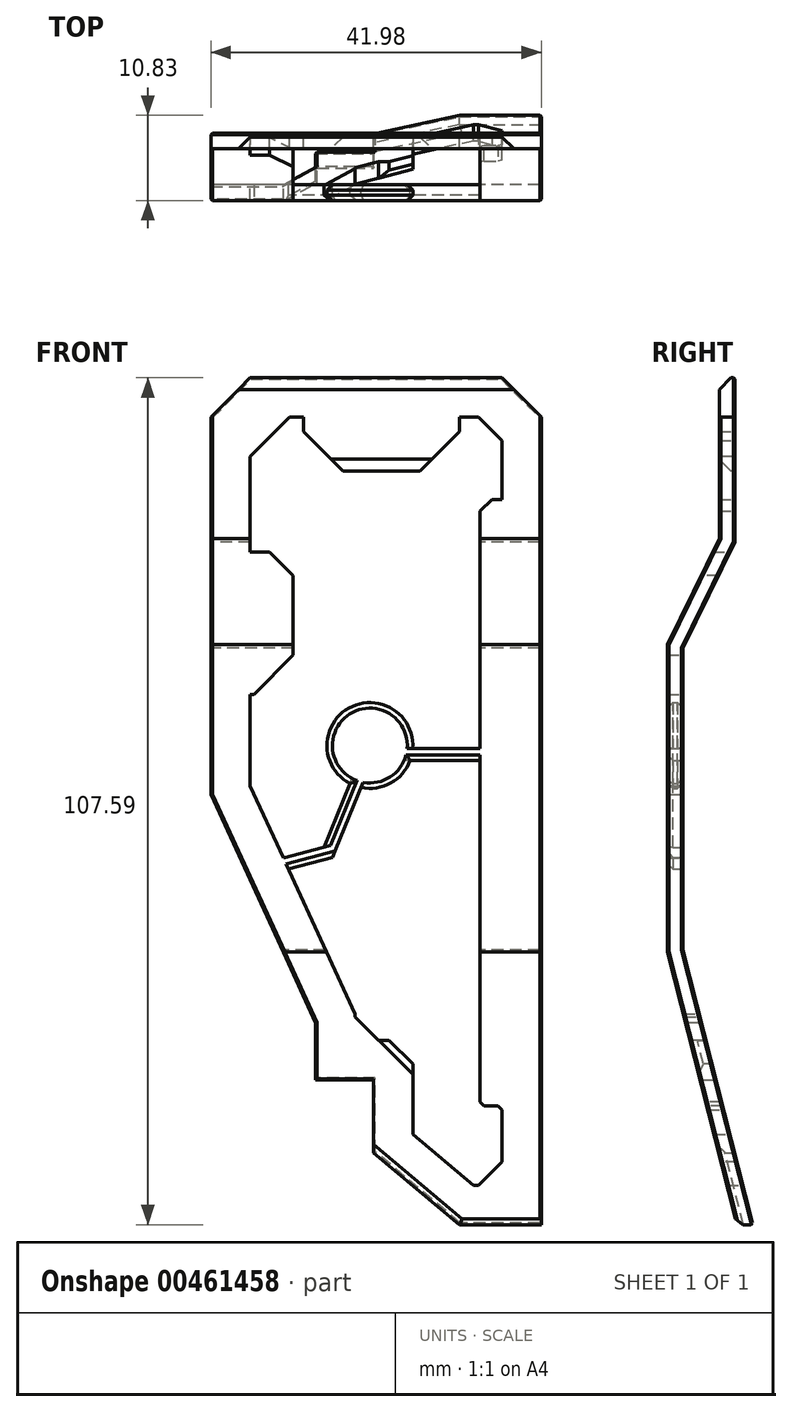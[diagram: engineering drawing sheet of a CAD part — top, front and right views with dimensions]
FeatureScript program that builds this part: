
annotation { "Feature Type Name" : "Feature", "Feature Type Description" : "" }
export const myFeature = defineFeature(function(context is Context, id is Id, definition is map)
    precondition{}
    {
        {
            var Q0;
            Q0=qCreatedBy(makeId("Front.planeOp"),FACE);
            var sketch = newSketch(context, id + "F0", { "sketchPlane" : qUnion([Q0])});
            skLineSegment(sketch, "E0", {"start": v(-31.56, 59.34) * mm, "end": v(-31.56, 0) * mm});
            skLineSegment(sketch, "E1", {"start": v(-31.56, 0) * mm, "end": v(-18.26, -28.95) * mm});
            skLineSegment(sketch, "E2", {"start": v(-18.26, -28.95) * mm, "end": v(-18.26, -36.23) * mm});
            skLineSegment(sketch, "E3", {"start": v(-18.26, -36.23) * mm, "end": v(-10.9, -36.23) * mm});
            skLineSegment(sketch, "E4", {"start": v(-10.9, -36.23) * mm, "end": v(-10.9, -45.5) * mm});
            skLineSegment(sketch, "E5", {"start": v(-10.9, -45.5) * mm, "end": v(0, -54.63) * mm});
            skLineSegment(sketch, "E6", {"start": v(0, -54.63) * mm, "end": v(10.42, -54.63) * mm});
            skLineSegment(sketch, "E7", {"start": v(10.42, -54.63) * mm, "end": v(10.42, 59.87) * mm});
            skLineSegment(sketch, "E8", {"start": v(-37.67, 52.96) * mm, "end": v(18.58, 52.96) * mm});
            skSolve(sketch);
        }
        {
            var Q0;
            Q0 = qSketchRegion(id + "F0", true);
            extrude(context, id + "F1", {"entities" : qUnion([Q0]), "depth" : 25.4 * mm});
        }
        {
            var Q0;
            Q0=qCreatedBy(makeId("Front.planeOp"),FACE);
            var sketch = newSketch(context, id + "F2", { "sketchPlane" : qUnion([Q0])});
            skLineSegment(sketch, "E9.0", {"start": v(-26.56, 47.96) * mm, "end": v(-26.56, 1.1) * mm});
            skLineSegment(sketch, "E9.1", {"start": v(-26.56, 1.1) * mm, "end": v(-13.26, -27.86) * mm});
            skLineSegment(sketch, "E9.2", {"start": v(-26.56, 47.96) * mm, "end": v(5.42, 47.96) * mm});
            skLineSegment(sketch, "E9.3", {"start": v(-13.26, -27.86) * mm, "end": v(-13.26, -31.23) * mm});
            skLineSegment(sketch, "E9.4", {"start": v(-13.26, -31.23) * mm, "end": v(-5.9, -31.23) * mm});
            skLineSegment(sketch, "E9.5", {"start": v(5.42, -49.63) * mm, "end": v(5.42, 47.96) * mm});
            skLineSegment(sketch, "E9.6", {"start": v(1.82, -49.63) * mm, "end": v(5.42, -49.63) * mm});
            skLineSegment(sketch, "E9.7", {"start": v(-5.9, -43.16) * mm, "end": v(1.82, -49.63) * mm});
            skLineSegment(sketch, "E9.8", {"start": v(-5.9, -31.23) * mm, "end": v(-5.9, -43.16) * mm});
            skLineSegment(sketch, "E10.bottom", {"start": v(-19.8, 63.96) * mm, "end": v(0, 63.96) * mm});
            skLineSegment(sketch, "E10.top", {"start": v(-19.8, 41.13) * mm, "end": v(0, 41.13) * mm});
            skLineSegment(sketch, "E10.left", {"start": v(-19.8, 63.96) * mm, "end": v(-19.8, 41.13) * mm});
            skLineSegment(sketch, "E10.right", {"start": v(0, 63.96) * mm, "end": v(0, 41.13) * mm});
            skLineSegment(sketch, "E11.bottom", {"start": v(-36.17, 30.84) * mm, "end": v(-21.1, 30.84) * mm});
            skLineSegment(sketch, "E11.top", {"start": v(-36.17, 12.73) * mm, "end": v(-21.1, 12.73) * mm});
            skLineSegment(sketch, "E11.left", {"start": v(-36.17, 30.84) * mm, "end": v(-36.17, 12.73) * mm});
            skLineSegment(sketch, "E11.right", {"start": v(-21.1, 30.84) * mm, "end": v(-21.1, 12.73) * mm});
            skLineSegment(sketch, "E12.bottom", {"start": v(15.3, -39.52) * mm, "end": v(2.65, -39.52) * mm});
            skLineSegment(sketch, "E12.top", {"start": v(15.3, 37.5) * mm, "end": v(2.65, 37.5) * mm});
            skLineSegment(sketch, "E12.left", {"start": v(15.3, -39.52) * mm, "end": v(15.3, 37.5) * mm});
            skLineSegment(sketch, "E12.right", {"start": v(2.65, -39.52) * mm, "end": v(2.65, 37.5) * mm});
            skCircle(sketch, "E13", {"center": v(-11.36, 6.24) * mm, "radius": 5.46 * mm});
            skLineSegment(sketch, "E14", {"start": v(-29.17, -9.83) * mm, "end": v(-17.21, -6.7) * mm});
            skLineSegment(sketch, "E15", {"start": v(-17.21, -6.7) * mm, "end": v(-12.54, 4.7) * mm});
            skLineSegment(sketch, "E16", {"start": v(-9.3, 5.86) * mm, "end": v(5.42, 5.86) * mm});
            skLineSegment(sketch, "E17.0", {"start": v(-16.11, -7.97) * mm, "end": v(-11.15, 4.13) * mm});
            skLineSegment(sketch, "E17.1", {"start": v(-28.8, -11.29) * mm, "end": v(-16.11, -7.97) * mm});
            skLineSegment(sketch, "E18.0", {"start": v(-9.3, 4.36) * mm, "end": v(5.42, 4.36) * mm});
            skLineSegment(sketch, "E19", {"start": v(-12.54, 4.7) * mm, "end": v(-11.15, 4.13) * mm});
            skLineSegment(sketch, "E20", {"start": v(-9.3, 5.86) * mm, "end": v(-9.3, 4.36) * mm});
            skLineSegment(sketch, "E21", {"start": v(-29.17, -9.83) * mm, "end": v(-29.17, -9.83) * mm});
            skLineSegment(sketch, "E22", {"start": v(-29.17, -9.83) * mm, "end": v(-28.8, -11.29) * mm});
            skLineSegment(sketch, "E23", {"start": v(5.42, 5.86) * mm, "end": v(5.42, 4.36) * mm});
            skSolve(sketch);
        }
        {
            var Q0;
            {var subQ1=sQuery(id+"F2.wireOp",EDGE,"E10.top");Q0=makeQuery(id+"F2.imprint","IMPRINT",FACE,{"disambiguationData":[TD([[makeQuery(id+"F2.imprint","IMPRINT",EDGE,{"derivedFrom":subQ1}),-1.0]])]});}
            extrude(context, id + "F3", {"entities" : qUnion([Q0]), "endBound" : BoundingType.SYMMETRIC, "depth" : 60 * mm});
        }
        {
            var Q0;
            {var subQ10=sQuery(id+"F2.wireOp",EDGE,"E9.3");Q0=makeQuery(id+"F2.imprint","IMPRINT",FACE,{"disambiguationData":[TD([[makeQuery(id+"F2.imprint","IMPRINT",EDGE,{"derivedFrom":subQ10}),1.0]])]});}
            extrude(context, id + "F4", {"entities" : qUnion([Q0]), "endBound" : BoundingType.SYMMETRIC, "depth" : 60 * mm});
        }
        {
            var Q0;
            Q0=makeQuery(id+"F3.opExtrude","SWEPT_BODY",BODY,{"disambiguationData":[OSD([sQuery(id+"F2.wireOp",EDGE,"E9.0"),sQuery(id+"F2.wireOp",EDGE,"E9.1"),sQuery(id+"F2.wireOp",EDGE,"E9.2"),sQuery(id+"F2.wireOp",EDGE,"E9.5"),sQuery(id+"F2.wireOp",EDGE,"E10.top"),sQuery(id+"F2.wireOp",EDGE,"E10.left"),sQuery(id+"F2.wireOp",EDGE,"E10.right"),sQuery(id+"F2.wireOp",EDGE,"E11.bottom"),sQuery(id+"F2.wireOp",EDGE,"E11.top"),sQuery(id+"F2.wireOp",EDGE,"E11.right"),sQuery(id+"F2.wireOp",EDGE,"E12.top"),sQuery(id+"F2.wireOp",EDGE,"E12.right"),sQuery(id+"F2.wireOp",EDGE,"E13"),sQuery(id+"F2.wireOp",EDGE,"E14"),sQuery(id+"F2.wireOp",EDGE,"E15"),sQuery(id+"F2.wireOp",EDGE,"E16")])]});
            var Q1;
            Q1=makeQuery(id+"F1.opExtrude","SWEPT_BODY",BODY,{"disambiguationData":[OSD([sQuery(id+"F0.wireOp",EDGE,"E0"),sQuery(id+"F0.wireOp",EDGE,"E1"),sQuery(id+"F0.wireOp",EDGE,"E2"),sQuery(id+"F0.wireOp",EDGE,"E3"),sQuery(id+"F0.wireOp",EDGE,"E4"),sQuery(id+"F0.wireOp",EDGE,"E5"),sQuery(id+"F0.wireOp",EDGE,"E6"),sQuery(id+"F0.wireOp",EDGE,"E7"),sQuery(id+"F0.wireOp",EDGE,"E8")])]});
            booleanBodies(context, id + "F5", {"operationType" : BooleanOperationType.SUBTRACTION, "tools" : qUnion([Q0]), "targets" : qUnion([Q1])});
        }
        {
            var Q0;
            Q0=makeQuery(id+"F4.opExtrude","SWEPT_BODY",BODY,{"disambiguationData":[OSD([sQuery(id+"F2.wireOp",EDGE,"E9.1"),sQuery(id+"F2.wireOp",EDGE,"E9.3"),sQuery(id+"F2.wireOp",EDGE,"E9.4"),sQuery(id+"F2.wireOp",EDGE,"E9.5"),sQuery(id+"F2.wireOp",EDGE,"E9.6"),sQuery(id+"F2.wireOp",EDGE,"E9.7"),sQuery(id+"F2.wireOp",EDGE,"E9.8"),sQuery(id+"F2.wireOp",EDGE,"E12.bottom"),sQuery(id+"F2.wireOp",EDGE,"E12.right"),sQuery(id+"F2.wireOp",EDGE,"E13"),sQuery(id+"F2.wireOp",EDGE,"E17.0"),sQuery(id+"F2.wireOp",EDGE,"E17.1"),sQuery(id+"F2.wireOp",EDGE,"E18.0")])]});
            var Q1;
            Q1=makeQuery(id+"F1.opExtrude","SWEPT_BODY",BODY,{"disambiguationData":[OSD([sQuery(id+"F0.wireOp",EDGE,"E0"),sQuery(id+"F0.wireOp",EDGE,"E1"),sQuery(id+"F0.wireOp",EDGE,"E2"),sQuery(id+"F0.wireOp",EDGE,"E3"),sQuery(id+"F0.wireOp",EDGE,"E4"),sQuery(id+"F0.wireOp",EDGE,"E5"),sQuery(id+"F0.wireOp",EDGE,"E6"),sQuery(id+"F0.wireOp",EDGE,"E7"),sQuery(id+"F0.wireOp",EDGE,"E8")])]});
            booleanBodies(context, id + "F6", {"operationType" : BooleanOperationType.SUBTRACTION, "tools" : qUnion([Q0]), "targets" : qUnion([Q1])});
        }
        {
            var Q0;
            Q0=makeQuery(id+"F1.opExtrude","CAP_FACE",FACE,{"disambiguationData":[OSD([sQuery(id+"F0.wireOp",EDGE,"E0"),sQuery(id+"F0.wireOp",EDGE,"E1"),sQuery(id+"F0.wireOp",EDGE,"E2"),sQuery(id+"F0.wireOp",EDGE,"E3"),sQuery(id+"F0.wireOp",EDGE,"E4"),sQuery(id+"F0.wireOp",EDGE,"E5"),sQuery(id+"F0.wireOp",EDGE,"E6"),sQuery(id+"F0.wireOp",EDGE,"E7"),sQuery(id+"F0.wireOp",EDGE,"E8")])],"isStart":true});
            extrude(context, id + "F7", {"entities" : qUnion([Q0]), "operationType" : NewBodyOperationType.ADD, "depth" : 25 * mm});
        }
        {
            var Q0;
            Q0=qCreatedBy(makeId("Right.planeOp"),FACE);
            var sketch = newSketch(context, id + "F8", { "sketchPlane" : qUnion([Q0])});
            skLineSegment(sketch, "E24", {"start": v(-5.44, 63.21) * mm, "end": v(-5.44, 32.1) * mm});
            skLineSegment(sketch, "E25", {"start": v(-5.44, 32.1) * mm, "end": v(-12.03, 18.6) * mm});
            skLineSegment(sketch, "E26", {"start": v(-12.03, 18.6) * mm, "end": v(-12.03, -19.71) * mm});
            skLineSegment(sketch, "E27", {"start": v(-12.03, -19.71) * mm, "end": v(-1.98, -59.15) * mm});
            skLineSegment(sketch, "E28.0", {"start": v(-14.03, -19.96) * mm, "end": v(-3.92, -59.64) * mm});
            skLineSegment(sketch, "E28.1", {"start": v(-14.03, 19.06) * mm, "end": v(-14.03, -19.96) * mm});
            skLineSegment(sketch, "E28.2", {"start": v(-7.44, 32.55) * mm, "end": v(-14.03, 19.06) * mm});
            skLineSegment(sketch, "E28.3", {"start": v(-7.44, 63.21) * mm, "end": v(-7.44, 32.55) * mm});
            skLineSegment(sketch, "E29", {"start": v(-5.44, 63.21) * mm, "end": v(-7.44, 63.21) * mm});
            skLineSegment(sketch, "E30", {"start": v(-1.98, -59.15) * mm, "end": v(-3.92, -59.64) * mm});
            skSolve(sketch);
        }
        {
            var Q0;
            Q0=makeQuery(id+"F8.imprint","IMPRINT",FACE,{"disambiguationData":[TD([[makeQuery(id+"F8.imprint","IMPRINT",EDGE,{"derivedFrom":sQuery(id+"F8.wireOp",EDGE,"E24")}),-1.0]])]});
            extrude(context, id + "F9", {"entities" : qUnion([Q0]), "endBound" : BoundingType.SYMMETRIC, "depth" : 80 * mm});
        }
        {
            var Q0;
            Q0=makeQuery(id+"F1.opExtrude","SWEPT_BODY",BODY,{"disambiguationData":[OSD([sQuery(id+"F0.wireOp",EDGE,"E0"),sQuery(id+"F0.wireOp",EDGE,"E1"),sQuery(id+"F0.wireOp",EDGE,"E2"),sQuery(id+"F0.wireOp",EDGE,"E3"),sQuery(id+"F0.wireOp",EDGE,"E4"),sQuery(id+"F0.wireOp",EDGE,"E5"),sQuery(id+"F0.wireOp",EDGE,"E6"),sQuery(id+"F0.wireOp",EDGE,"E7"),sQuery(id+"F0.wireOp",EDGE,"E8")])]});
            var Q1;
            Q1=makeQuery(id+"F9.opExtrude","SWEPT_BODY",BODY,{"disambiguationData":[OSD([sQuery(id+"F8.wireOp",EDGE,"E24"),sQuery(id+"F8.wireOp",EDGE,"E25"),sQuery(id+"F8.wireOp",EDGE,"E26"),sQuery(id+"F8.wireOp",EDGE,"E27"),sQuery(id+"F8.wireOp",EDGE,"E28.0"),sQuery(id+"F8.wireOp",EDGE,"E28.1"),sQuery(id+"F8.wireOp",EDGE,"E28.2"),sQuery(id+"F8.wireOp",EDGE,"E28.3"),sQuery(id+"F8.wireOp",EDGE,"E29"),sQuery(id+"F8.wireOp",EDGE,"E30")])]});
            booleanBodies(context, id + "F10", {"operationType" : BooleanOperationType.INTERSECTION, "tools" : qUnion([Q0, Q1])});
        }
        {
            var Q0;
            {var subQ0=sQuery(id+"F2.wireOp",EDGE,"E9.2");var subQ1=sQuery(id+"F2.wireOp",EDGE,"E9.0");Q0=makeQuery(id+"F7.boolean.opBoolean","MERGE",EDGE,{"derivedFrom":[makeQuery(id+"F5.opBoolean","COPY",EDGE,{"derivedFrom":makeQuery(id+"F3.opExtrude","SWEPT_EDGE",EDGE,{"disambiguationData":[OSD([subQ1,subQ0])]})}),makeQuery(id+"F7.opExtrude","SWEPT_EDGE",EDGE,{"disambiguationData":[OSD([sQuery(id+"F0.wireOp",EDGE,"E0"),sQuery(id+"F0.wireOp",EDGE,"E1"),sQuery(id+"F0.wireOp",EDGE,"E2"),sQuery(id+"F0.wireOp",EDGE,"E3"),sQuery(id+"F0.wireOp",EDGE,"E4"),sQuery(id+"F0.wireOp",EDGE,"E5"),sQuery(id+"F0.wireOp",EDGE,"E6"),sQuery(id+"F0.wireOp",EDGE,"E7"),sQuery(id+"F0.wireOp",EDGE,"E8"),subQ1,subQ0])]})]});}
            var Q1;
            {var subQ0=sQuery(id+"F2.wireOp",EDGE,"E10.right");var subQ1=sQuery(id+"F2.wireOp",EDGE,"E10.top");Q1=makeQuery(id+"F7.boolean.opBoolean","MERGE",EDGE,{"derivedFrom":[makeQuery(id+"F5.opBoolean","COPY",EDGE,{"derivedFrom":makeQuery(id+"F3.opExtrude","SWEPT_EDGE",EDGE,{"disambiguationData":[OSD([subQ1,subQ0])]})}),makeQuery(id+"F7.opExtrude","SWEPT_EDGE",EDGE,{"disambiguationData":[OSD([sQuery(id+"F0.wireOp",EDGE,"E0"),sQuery(id+"F0.wireOp",EDGE,"E1"),sQuery(id+"F0.wireOp",EDGE,"E2"),sQuery(id+"F0.wireOp",EDGE,"E3"),sQuery(id+"F0.wireOp",EDGE,"E4"),sQuery(id+"F0.wireOp",EDGE,"E5"),sQuery(id+"F0.wireOp",EDGE,"E6"),sQuery(id+"F0.wireOp",EDGE,"E7"),sQuery(id+"F0.wireOp",EDGE,"E8"),subQ1,subQ0])]})]});}
            var Q2;
            {var subQ0=sQuery(id+"F2.wireOp",EDGE,"E10.left");var subQ1=sQuery(id+"F2.wireOp",EDGE,"E10.top");Q2=makeQuery(id+"F7.boolean.opBoolean","MERGE",EDGE,{"derivedFrom":[makeQuery(id+"F5.opBoolean","COPY",EDGE,{"derivedFrom":makeQuery(id+"F3.opExtrude","SWEPT_EDGE",EDGE,{"disambiguationData":[OSD([subQ1,subQ0])]})}),makeQuery(id+"F7.opExtrude","SWEPT_EDGE",EDGE,{"disambiguationData":[OSD([sQuery(id+"F0.wireOp",EDGE,"E0"),sQuery(id+"F0.wireOp",EDGE,"E1"),sQuery(id+"F0.wireOp",EDGE,"E2"),sQuery(id+"F0.wireOp",EDGE,"E3"),sQuery(id+"F0.wireOp",EDGE,"E4"),sQuery(id+"F0.wireOp",EDGE,"E5"),sQuery(id+"F0.wireOp",EDGE,"E6"),sQuery(id+"F0.wireOp",EDGE,"E7"),sQuery(id+"F0.wireOp",EDGE,"E8"),subQ1,subQ0])]})]});}
            var Q3;
            {var subQ0=sQuery(id+"F2.wireOp",EDGE,"E11.right");var subQ1=sQuery(id+"F2.wireOp",EDGE,"E11.top");Q3=makeQuery(id+"F7.boolean.opBoolean","MERGE",EDGE,{"derivedFrom":[makeQuery(id+"F5.opBoolean","COPY",EDGE,{"derivedFrom":makeQuery(id+"F3.opExtrude","SWEPT_EDGE",EDGE,{"disambiguationData":[OSD([subQ1,subQ0])]})}),makeQuery(id+"F7.opExtrude","SWEPT_EDGE",EDGE,{"disambiguationData":[OSD([sQuery(id+"F0.wireOp",EDGE,"E0"),sQuery(id+"F0.wireOp",EDGE,"E1"),sQuery(id+"F0.wireOp",EDGE,"E2"),sQuery(id+"F0.wireOp",EDGE,"E3"),sQuery(id+"F0.wireOp",EDGE,"E4"),sQuery(id+"F0.wireOp",EDGE,"E5"),sQuery(id+"F0.wireOp",EDGE,"E6"),sQuery(id+"F0.wireOp",EDGE,"E7"),sQuery(id+"F0.wireOp",EDGE,"E8"),subQ1,subQ0])]})]});}
            chamfer(context, id + "F11", {"entities" : qUnion([Q0, Q1, Q2, Q3]), "width" : 5 * mm, "tangentPropagation" : true});
        }
        {
            var Q0;
            {var subQ0=sQuery(id+"F2.wireOp",EDGE,"E9.5");var subQ1=sQuery(id+"F2.wireOp",EDGE,"E9.2");Q0=makeQuery(id+"F7.boolean.opBoolean","MERGE",EDGE,{"derivedFrom":[makeQuery(id+"F5.opBoolean","COPY",EDGE,{"derivedFrom":makeQuery(id+"F3.opExtrude","SWEPT_EDGE",EDGE,{"disambiguationData":[OSD([subQ1,subQ0])]})}),makeQuery(id+"F7.opExtrude","SWEPT_EDGE",EDGE,{"disambiguationData":[OSD([sQuery(id+"F0.wireOp",EDGE,"E0"),sQuery(id+"F0.wireOp",EDGE,"E1"),sQuery(id+"F0.wireOp",EDGE,"E2"),sQuery(id+"F0.wireOp",EDGE,"E3"),sQuery(id+"F0.wireOp",EDGE,"E4"),sQuery(id+"F0.wireOp",EDGE,"E5"),sQuery(id+"F0.wireOp",EDGE,"E6"),sQuery(id+"F0.wireOp",EDGE,"E7"),sQuery(id+"F0.wireOp",EDGE,"E8"),subQ1,subQ0])]})]});}
            var Q1;
            {var subQ0=sQuery(id+"F2.wireOp",EDGE,"E11.right");var subQ1=sQuery(id+"F2.wireOp",EDGE,"E11.bottom");Q1=makeQuery(id+"F7.boolean.opBoolean","MERGE",EDGE,{"derivedFrom":[makeQuery(id+"F5.opBoolean","COPY",EDGE,{"derivedFrom":makeQuery(id+"F3.opExtrude","SWEPT_EDGE",EDGE,{"disambiguationData":[OSD([subQ1,subQ0])]})}),makeQuery(id+"F7.opExtrude","SWEPT_EDGE",EDGE,{"disambiguationData":[OSD([sQuery(id+"F0.wireOp",EDGE,"E0"),sQuery(id+"F0.wireOp",EDGE,"E1"),sQuery(id+"F0.wireOp",EDGE,"E2"),sQuery(id+"F0.wireOp",EDGE,"E3"),sQuery(id+"F0.wireOp",EDGE,"E4"),sQuery(id+"F0.wireOp",EDGE,"E5"),sQuery(id+"F0.wireOp",EDGE,"E6"),sQuery(id+"F0.wireOp",EDGE,"E7"),sQuery(id+"F0.wireOp",EDGE,"E8"),subQ1,subQ0])]})]});}
            var Q2;
            {var subQ0=sQuery(id+"F2.wireOp",EDGE,"E9.6");var subQ1=sQuery(id+"F2.wireOp",EDGE,"E9.5");Q2=makeQuery(id+"F7.boolean.opBoolean","MERGE",EDGE,{"derivedFrom":[makeQuery(id+"F6.opBoolean","COPY",EDGE,{"derivedFrom":makeQuery(id+"F4.opExtrude","SWEPT_EDGE",EDGE,{"disambiguationData":[OSD([subQ1,subQ0])]})}),makeQuery(id+"F7.opExtrude","SWEPT_EDGE",EDGE,{"disambiguationData":[OSD([sQuery(id+"F0.wireOp",EDGE,"E0"),sQuery(id+"F0.wireOp",EDGE,"E1"),sQuery(id+"F0.wireOp",EDGE,"E2"),sQuery(id+"F0.wireOp",EDGE,"E3"),sQuery(id+"F0.wireOp",EDGE,"E4"),sQuery(id+"F0.wireOp",EDGE,"E5"),sQuery(id+"F0.wireOp",EDGE,"E6"),sQuery(id+"F0.wireOp",EDGE,"E7"),sQuery(id+"F0.wireOp",EDGE,"E8"),subQ1,subQ0])]})]});}
            var Q3;
            {var subQ0=sQuery(id+"F2.wireOp",EDGE,"E9.8");var subQ1=sQuery(id+"F2.wireOp",EDGE,"E9.4");Q3=makeQuery(id+"F7.boolean.opBoolean","MERGE",EDGE,{"derivedFrom":[makeQuery(id+"F6.opBoolean","COPY",EDGE,{"derivedFrom":makeQuery(id+"F4.opExtrude","SWEPT_EDGE",EDGE,{"disambiguationData":[OSD([subQ1,subQ0])]})}),makeQuery(id+"F7.opExtrude","SWEPT_EDGE",EDGE,{"disambiguationData":[OSD([sQuery(id+"F0.wireOp",EDGE,"E0"),sQuery(id+"F0.wireOp",EDGE,"E1"),sQuery(id+"F0.wireOp",EDGE,"E2"),sQuery(id+"F0.wireOp",EDGE,"E3"),sQuery(id+"F0.wireOp",EDGE,"E4"),sQuery(id+"F0.wireOp",EDGE,"E5"),sQuery(id+"F0.wireOp",EDGE,"E6"),sQuery(id+"F0.wireOp",EDGE,"E7"),sQuery(id+"F0.wireOp",EDGE,"E8"),subQ1,subQ0])]})]});}
            var Q4;
            {var subQ0=sQuery(id+"F2.wireOp",EDGE,"E9.4");var subQ1=sQuery(id+"F2.wireOp",EDGE,"E9.3");Q4=makeQuery(id+"F7.boolean.opBoolean","MERGE",EDGE,{"derivedFrom":[makeQuery(id+"F6.opBoolean","COPY",EDGE,{"derivedFrom":makeQuery(id+"F4.opExtrude","SWEPT_EDGE",EDGE,{"disambiguationData":[OSD([subQ1,subQ0])]})}),makeQuery(id+"F7.opExtrude","SWEPT_EDGE",EDGE,{"disambiguationData":[OSD([sQuery(id+"F0.wireOp",EDGE,"E0"),sQuery(id+"F0.wireOp",EDGE,"E1"),sQuery(id+"F0.wireOp",EDGE,"E2"),sQuery(id+"F0.wireOp",EDGE,"E3"),sQuery(id+"F0.wireOp",EDGE,"E4"),sQuery(id+"F0.wireOp",EDGE,"E5"),sQuery(id+"F0.wireOp",EDGE,"E6"),sQuery(id+"F0.wireOp",EDGE,"E7"),sQuery(id+"F0.wireOp",EDGE,"E8"),subQ1,subQ0])]})]});}
            chamfer(context, id + "F12", {"entities" : qUnion([Q0, Q1, Q2, Q3, Q4]), "width" : 3 * mm, "tangentPropagation" : true});
        }
        {
            var Q0;
            {var subQ0=sQuery(id+"F2.wireOp",EDGE,"E12.right");var subQ1=sQuery(id+"F2.wireOp",EDGE,"E12.top");Q0=makeQuery(id+"F7.boolean.opBoolean","MERGE",EDGE,{"derivedFrom":[makeQuery(id+"F5.opBoolean","COPY",EDGE,{"derivedFrom":makeQuery(id+"F3.opExtrude","SWEPT_EDGE",EDGE,{"disambiguationData":[OSD([subQ1,subQ0])]})}),makeQuery(id+"F7.opExtrude","SWEPT_EDGE",EDGE,{"disambiguationData":[OSD([sQuery(id+"F0.wireOp",EDGE,"E0"),sQuery(id+"F0.wireOp",EDGE,"E1"),sQuery(id+"F0.wireOp",EDGE,"E2"),sQuery(id+"F0.wireOp",EDGE,"E3"),sQuery(id+"F0.wireOp",EDGE,"E4"),sQuery(id+"F0.wireOp",EDGE,"E5"),sQuery(id+"F0.wireOp",EDGE,"E6"),sQuery(id+"F0.wireOp",EDGE,"E7"),sQuery(id+"F0.wireOp",EDGE,"E8"),subQ1,subQ0])]})]});}
            chamfer(context, id + "F13", {"entities" : qUnion([Q0]), "width" : 1.5 * mm, "tangentPropagation" : true});
        }
        {
            var Q0;
            {var subQ0=sQuery(id+"F0.wireOp",EDGE,"E8");var subQ1=sQuery(id+"F0.wireOp",EDGE,"E7");Q0=makeQuery(id+"F7.boolean.opBoolean","MERGE",EDGE,{"derivedFrom":[makeQuery(id+"F1.opExtrude","SWEPT_EDGE",EDGE,{"disambiguationData":[OSD([subQ1,subQ0])]}),makeQuery(id+"F7.opExtrude","SWEPT_EDGE",EDGE,{"disambiguationData":[OSD([subQ1,subQ0])]})]});}
            var Q1;
            {var subQ0=sQuery(id+"F0.wireOp",EDGE,"E8");var subQ1=sQuery(id+"F0.wireOp",EDGE,"E0");Q1=makeQuery(id+"F7.boolean.opBoolean","MERGE",EDGE,{"derivedFrom":[makeQuery(id+"F1.opExtrude","SWEPT_EDGE",EDGE,{"disambiguationData":[OSD([subQ1,subQ0])]}),makeQuery(id+"F7.opExtrude","SWEPT_EDGE",EDGE,{"disambiguationData":[OSD([subQ1,subQ0])]})]});}
            chamfer(context, id + "F14", {"entities" : qUnion([Q0, Q1]), "width" : 5 * mm, "tangentPropagation" : true});
        }
        {
            var Q0;
            {var subQ0=sQuery(id+"F2.wireOp",EDGE,"E13");var subQ1=makeQuery(id+"F3.opExtrude","SWEPT_FACE",FACE,{"disambiguationData":[OSD([subQ0])]});var subQ2=sQuery(id+"F0.wireOp",EDGE,"E8");var subQ3=sQuery(id+"F0.wireOp",EDGE,"E7");var subQ4=sQuery(id+"F0.wireOp",EDGE,"E6");var subQ5=sQuery(id+"F0.wireOp",EDGE,"E5");var subQ6=sQuery(id+"F0.wireOp",EDGE,"E4");var subQ7=sQuery(id+"F0.wireOp",EDGE,"E3");var subQ8=sQuery(id+"F0.wireOp",EDGE,"E2");var subQ9=sQuery(id+"F0.wireOp",EDGE,"E1");var subQ10=sQuery(id+"F0.wireOp",EDGE,"E0");Q0=makeQuery(id+"F10.opBoolean","INTERSECT",EDGE,{"derivedFrom":[makeQuery(id+"F7.boolean.opBoolean","MERGE",FACE,{"derivedFrom":[makeQuery(id+"F5.opBoolean","COPY",FACE,{"derivedFrom":subQ1}),makeQuery(id+"F7.opExtrude","SWEPT_FACE",FACE,{"disambiguationData":[OSD([subQ10,subQ9,subQ8,subQ7,subQ6,subQ5,subQ4,subQ3,subQ2,subQ0]),TDD([makeQuery(id+"F5.opBoolean","INTERSECT",EDGE,{"derivedFrom":[makeQuery(id+"F1.opExtrude","CAP_FACE",FACE,{"disambiguationData":[OSD([subQ10,subQ9,subQ8,subQ7,subQ6,subQ5,subQ4,subQ3,subQ2])],"isStart":true}),subQ1]})])]})]}),makeQuery(id+"F9.opExtrude","SWEPT_FACE",FACE,{"disambiguationData":[OSD([sQuery(id+"F8.wireOp",EDGE,"E26")])]})]});}
            var Q1;
            {var subQ0=sQuery(id+"F0.wireOp",EDGE,"E8");var subQ1=sQuery(id+"F0.wireOp",EDGE,"E7");var subQ2=sQuery(id+"F0.wireOp",EDGE,"E6");var subQ3=sQuery(id+"F0.wireOp",EDGE,"E5");var subQ4=sQuery(id+"F0.wireOp",EDGE,"E4");var subQ5=sQuery(id+"F0.wireOp",EDGE,"E3");var subQ6=sQuery(id+"F0.wireOp",EDGE,"E2");var subQ7=sQuery(id+"F0.wireOp",EDGE,"E1");var subQ8=sQuery(id+"F0.wireOp",EDGE,"E0");var subQ9=sQuery(id+"F2.wireOp",EDGE,"E13");var subQ10=makeQuery(id+"F4.opExtrude","SWEPT_FACE",FACE,{"disambiguationData":[OSD([subQ9])]});Q1=makeQuery(id+"F10.opBoolean","INTERSECT",EDGE,{"derivedFrom":[makeQuery(id+"F7.boolean.opBoolean","MERGE",FACE,{"derivedFrom":[makeQuery(id+"F6.opBoolean","COPY",FACE,{"derivedFrom":subQ10}),makeQuery(id+"F7.opExtrude","SWEPT_FACE",FACE,{"disambiguationData":[OSD([subQ8,subQ7,subQ6,subQ5,subQ4,subQ3,subQ2,subQ1,subQ0,subQ9]),TDD([makeQuery(id+"F6.opBoolean","INTERSECT",EDGE,{"derivedFrom":[subQ10,makeQuery(id+"F1.opExtrude","CAP_FACE",FACE,{"disambiguationData":[OSD([subQ8,subQ7,subQ6,subQ5,subQ4,subQ3,subQ2,subQ1,subQ0])],"isStart":true})]})])]})]}),makeQuery(id+"F9.opExtrude","SWEPT_FACE",FACE,{"disambiguationData":[OSD([sQuery(id+"F8.wireOp",EDGE,"E26")])]})]});}
            var Q2;
            {var subQ0=sQuery(id+"F2.wireOp",EDGE,"E13");var subQ1=makeQuery(id+"F3.opExtrude","SWEPT_FACE",FACE,{"disambiguationData":[OSD([subQ0])]});var subQ2=sQuery(id+"F0.wireOp",EDGE,"E8");var subQ3=sQuery(id+"F0.wireOp",EDGE,"E7");var subQ4=sQuery(id+"F0.wireOp",EDGE,"E6");var subQ5=sQuery(id+"F0.wireOp",EDGE,"E5");var subQ6=sQuery(id+"F0.wireOp",EDGE,"E4");var subQ7=sQuery(id+"F0.wireOp",EDGE,"E3");var subQ8=sQuery(id+"F0.wireOp",EDGE,"E2");var subQ9=sQuery(id+"F0.wireOp",EDGE,"E1");var subQ10=sQuery(id+"F0.wireOp",EDGE,"E0");Q2=makeQuery(id+"F10.opBoolean","INTERSECT",EDGE,{"derivedFrom":[makeQuery(id+"F7.boolean.opBoolean","MERGE",FACE,{"derivedFrom":[makeQuery(id+"F5.opBoolean","COPY",FACE,{"derivedFrom":subQ1}),makeQuery(id+"F7.opExtrude","SWEPT_FACE",FACE,{"disambiguationData":[OSD([subQ10,subQ9,subQ8,subQ7,subQ6,subQ5,subQ4,subQ3,subQ2,subQ0]),TDD([makeQuery(id+"F5.opBoolean","INTERSECT",EDGE,{"derivedFrom":[makeQuery(id+"F1.opExtrude","CAP_FACE",FACE,{"disambiguationData":[OSD([subQ10,subQ9,subQ8,subQ7,subQ6,subQ5,subQ4,subQ3,subQ2])],"isStart":true}),subQ1]})])]})]}),makeQuery(id+"F9.opExtrude","SWEPT_FACE",FACE,{"disambiguationData":[OSD([sQuery(id+"F8.wireOp",EDGE,"E28.1")])]})]});}
            var Q3;
            {var subQ0=sQuery(id+"F0.wireOp",EDGE,"E8");var subQ1=sQuery(id+"F0.wireOp",EDGE,"E7");var subQ2=sQuery(id+"F0.wireOp",EDGE,"E6");var subQ3=sQuery(id+"F0.wireOp",EDGE,"E5");var subQ4=sQuery(id+"F0.wireOp",EDGE,"E4");var subQ5=sQuery(id+"F0.wireOp",EDGE,"E3");var subQ6=sQuery(id+"F0.wireOp",EDGE,"E2");var subQ7=sQuery(id+"F0.wireOp",EDGE,"E1");var subQ8=sQuery(id+"F0.wireOp",EDGE,"E0");var subQ9=sQuery(id+"F2.wireOp",EDGE,"E13");var subQ10=makeQuery(id+"F4.opExtrude","SWEPT_FACE",FACE,{"disambiguationData":[OSD([subQ9])]});Q3=makeQuery(id+"F10.opBoolean","INTERSECT",EDGE,{"derivedFrom":[makeQuery(id+"F7.boolean.opBoolean","MERGE",FACE,{"derivedFrom":[makeQuery(id+"F6.opBoolean","COPY",FACE,{"derivedFrom":subQ10}),makeQuery(id+"F7.opExtrude","SWEPT_FACE",FACE,{"disambiguationData":[OSD([subQ8,subQ7,subQ6,subQ5,subQ4,subQ3,subQ2,subQ1,subQ0,subQ9]),TDD([makeQuery(id+"F6.opBoolean","INTERSECT",EDGE,{"derivedFrom":[subQ10,makeQuery(id+"F1.opExtrude","CAP_FACE",FACE,{"disambiguationData":[OSD([subQ8,subQ7,subQ6,subQ5,subQ4,subQ3,subQ2,subQ1,subQ0])],"isStart":true})]})])]})]}),makeQuery(id+"F9.opExtrude","SWEPT_FACE",FACE,{"disambiguationData":[OSD([sQuery(id+"F8.wireOp",EDGE,"E28.1")])]})]});}
            var Q4;
            {var subQ0=sQuery(id+"F2.wireOp",EDGE,"E15");Q4=makeQuery(id+"F10.opBoolean","INTERSECT",EDGE,{"derivedFrom":[makeQuery(id+"F7.boolean.opBoolean","MERGE",FACE,{"derivedFrom":[makeQuery(id+"F5.opBoolean","COPY",FACE,{"derivedFrom":makeQuery(id+"F3.opExtrude","SWEPT_FACE",FACE,{"disambiguationData":[OSD([subQ0])]})}),makeQuery(id+"F7.opExtrude","SWEPT_FACE",FACE,{"disambiguationData":[OSD([sQuery(id+"F0.wireOp",EDGE,"E0"),sQuery(id+"F0.wireOp",EDGE,"E1"),sQuery(id+"F0.wireOp",EDGE,"E2"),sQuery(id+"F0.wireOp",EDGE,"E3"),sQuery(id+"F0.wireOp",EDGE,"E4"),sQuery(id+"F0.wireOp",EDGE,"E5"),sQuery(id+"F0.wireOp",EDGE,"E6"),sQuery(id+"F0.wireOp",EDGE,"E7"),sQuery(id+"F0.wireOp",EDGE,"E8"),subQ0])]})]}),makeQuery(id+"F9.opExtrude","SWEPT_FACE",FACE,{"disambiguationData":[OSD([sQuery(id+"F8.wireOp",EDGE,"E28.1")])]})]});}
            var Q5;
            {var subQ0=sQuery(id+"F2.wireOp",EDGE,"E17.1");Q5=makeQuery(id+"F10.opBoolean","INTERSECT",EDGE,{"derivedFrom":[makeQuery(id+"F7.boolean.opBoolean","MERGE",FACE,{"derivedFrom":[makeQuery(id+"F6.opBoolean","COPY",FACE,{"derivedFrom":makeQuery(id+"F4.opExtrude","SWEPT_FACE",FACE,{"disambiguationData":[OSD([subQ0])]})}),makeQuery(id+"F7.opExtrude","SWEPT_FACE",FACE,{"disambiguationData":[OSD([sQuery(id+"F0.wireOp",EDGE,"E0"),sQuery(id+"F0.wireOp",EDGE,"E1"),sQuery(id+"F0.wireOp",EDGE,"E2"),sQuery(id+"F0.wireOp",EDGE,"E3"),sQuery(id+"F0.wireOp",EDGE,"E4"),sQuery(id+"F0.wireOp",EDGE,"E5"),sQuery(id+"F0.wireOp",EDGE,"E6"),sQuery(id+"F0.wireOp",EDGE,"E7"),sQuery(id+"F0.wireOp",EDGE,"E8"),subQ0])]})]}),makeQuery(id+"F9.opExtrude","SWEPT_FACE",FACE,{"disambiguationData":[OSD([sQuery(id+"F8.wireOp",EDGE,"E28.1")])]})]});}
            var Q6;
            {var subQ0=sQuery(id+"F2.wireOp",EDGE,"E18.0");Q6=makeQuery(id+"F10.opBoolean","INTERSECT",EDGE,{"derivedFrom":[makeQuery(id+"F7.boolean.opBoolean","MERGE",FACE,{"derivedFrom":[makeQuery(id+"F6.opBoolean","COPY",FACE,{"derivedFrom":makeQuery(id+"F4.opExtrude","SWEPT_FACE",FACE,{"disambiguationData":[OSD([subQ0])]})}),makeQuery(id+"F7.opExtrude","SWEPT_FACE",FACE,{"disambiguationData":[OSD([sQuery(id+"F0.wireOp",EDGE,"E0"),sQuery(id+"F0.wireOp",EDGE,"E1"),sQuery(id+"F0.wireOp",EDGE,"E2"),sQuery(id+"F0.wireOp",EDGE,"E3"),sQuery(id+"F0.wireOp",EDGE,"E4"),sQuery(id+"F0.wireOp",EDGE,"E5"),sQuery(id+"F0.wireOp",EDGE,"E6"),sQuery(id+"F0.wireOp",EDGE,"E7"),sQuery(id+"F0.wireOp",EDGE,"E8"),subQ0])]})]}),makeQuery(id+"F9.opExtrude","SWEPT_FACE",FACE,{"disambiguationData":[OSD([sQuery(id+"F8.wireOp",EDGE,"E28.1")])]})]});}
            chamfer(context, id + "F15", {"entities" : qUnion([Q0, Q1, Q2, Q3, Q4, Q5, Q6]), "width" : 0.7 * mm, "tangentPropagation" : true});
        }
        {
            var Q0;
            {var subQ0=sQuery(id+"F2.wireOp",EDGE,"E10.top");Q0=makeQuery(id+"F10.opBoolean","INTERSECT",EDGE,{"derivedFrom":[makeQuery(id+"F7.boolean.opBoolean","MERGE",FACE,{"derivedFrom":[makeQuery(id+"F5.opBoolean","COPY",FACE,{"derivedFrom":makeQuery(id+"F3.opExtrude","SWEPT_FACE",FACE,{"disambiguationData":[OSD([subQ0])]})}),makeQuery(id+"F7.opExtrude","SWEPT_FACE",FACE,{"disambiguationData":[OSD([sQuery(id+"F0.wireOp",EDGE,"E0"),sQuery(id+"F0.wireOp",EDGE,"E1"),sQuery(id+"F0.wireOp",EDGE,"E2"),sQuery(id+"F0.wireOp",EDGE,"E3"),sQuery(id+"F0.wireOp",EDGE,"E4"),sQuery(id+"F0.wireOp",EDGE,"E5"),sQuery(id+"F0.wireOp",EDGE,"E6"),sQuery(id+"F0.wireOp",EDGE,"E7"),sQuery(id+"F0.wireOp",EDGE,"E8"),subQ0])]})]}),makeQuery(id+"F9.opExtrude","SWEPT_FACE",FACE,{"disambiguationData":[OSD([sQuery(id+"F8.wireOp",EDGE,"E28.3")])]})]});}
            chamfer(context, id + "F16", {"entities" : qUnion([Q0]), "width" : 1.5 * mm, "tangentPropagation" : true});
        }
        {
            var Q0;
            {var subQ0=sQuery(id+"F0.wireOp",EDGE,"E8");Q0=makeQuery(id+"F10.opBoolean","INTERSECT",EDGE,{"derivedFrom":[makeQuery(id+"F7.boolean.opBoolean","MERGE",FACE,{"derivedFrom":[makeQuery(id+"F1.opExtrude","SWEPT_FACE",FACE,{"disambiguationData":[OSD([subQ0])]}),makeQuery(id+"F7.opExtrude","SWEPT_FACE",FACE,{"disambiguationData":[OSD([subQ0])]})]}),makeQuery(id+"F9.opExtrude","SWEPT_FACE",FACE,{"disambiguationData":[OSD([sQuery(id+"F8.wireOp",EDGE,"E28.3")])]})]});}
            chamfer(context, id + "F17", {"entities" : qUnion([Q0]), "width" : 1.5 * mm, "tangentPropagation" : true});
        }
        {
            var Q0;
            {var subQ0=sQuery(id+"F0.wireOp",EDGE,"E5");Q0=makeQuery(id+"F10.opBoolean","INTERSECT",EDGE,{"derivedFrom":[makeQuery(id+"F7.boolean.opBoolean","MERGE",FACE,{"derivedFrom":[makeQuery(id+"F1.opExtrude","SWEPT_FACE",FACE,{"disambiguationData":[OSD([subQ0])]}),makeQuery(id+"F7.opExtrude","SWEPT_FACE",FACE,{"disambiguationData":[OSD([subQ0])]})]}),makeQuery(id+"F9.opExtrude","SWEPT_FACE",FACE,{"disambiguationData":[OSD([sQuery(id+"F8.wireOp",EDGE,"E28.0")])]})]});}
            var Q1;
            {var subQ0=sQuery(id+"F0.wireOp",EDGE,"E6");Q1=makeQuery(id+"F10.opBoolean","INTERSECT",EDGE,{"derivedFrom":[makeQuery(id+"F7.boolean.opBoolean","MERGE",FACE,{"derivedFrom":[makeQuery(id+"F1.opExtrude","SWEPT_FACE",FACE,{"disambiguationData":[OSD([subQ0])]}),makeQuery(id+"F7.opExtrude","SWEPT_FACE",FACE,{"disambiguationData":[OSD([subQ0])]})]}),makeQuery(id+"F9.opExtrude","SWEPT_FACE",FACE,{"disambiguationData":[OSD([sQuery(id+"F8.wireOp",EDGE,"E28.0")])]})]});}
            chamfer(context, id + "F18", {"entities" : qUnion([Q0, Q1]), "width" : 1 * mm, "tangentPropagation" : true});
        }
        {
            var Q0;
            {var subQ0=sQuery(id+"F2.wireOp",EDGE,"E9.8");var subQ1=sQuery(id+"F2.wireOp",EDGE,"E9.4");Q0=makeQuery(id+"F12.opChamfer","BLEND_EDGE",EDGE,{"blendedFrom":[makeQuery(id+"F7.boolean.opBoolean","MERGE",EDGE,{"derivedFrom":[makeQuery(id+"F6.opBoolean","COPY",EDGE,{"derivedFrom":makeQuery(id+"F4.opExtrude","SWEPT_EDGE",EDGE,{"disambiguationData":[OSD([subQ1,subQ0])]})}),makeQuery(id+"F7.opExtrude","SWEPT_EDGE",EDGE,{"disambiguationData":[OSD([sQuery(id+"F0.wireOp",EDGE,"E0"),sQuery(id+"F0.wireOp",EDGE,"E1"),sQuery(id+"F0.wireOp",EDGE,"E2"),sQuery(id+"F0.wireOp",EDGE,"E3"),sQuery(id+"F0.wireOp",EDGE,"E4"),sQuery(id+"F0.wireOp",EDGE,"E5"),sQuery(id+"F0.wireOp",EDGE,"E6"),sQuery(id+"F0.wireOp",EDGE,"E7"),sQuery(id+"F0.wireOp",EDGE,"E8"),subQ1,subQ0])]})]}),makeQuery(id+"F9.opExtrude","SWEPT_FACE",FACE,{"disambiguationData":[OSD([sQuery(id+"F8.wireOp",EDGE,"E28.0")])]})],"blendedInto":[makeQuery(id+"F9.opExtrude","SWEPT_FACE",FACE,{"disambiguationData":[OSD([sQuery(id+"F8.wireOp",EDGE,"E28.0")])]})]});}
            chamfer(context, id + "F19", {"entities" : qUnion([Q0]), "width" : 0.8 * mm, "tangentPropagation" : true});
        }
        {
            var Q0;
            {var subQ0=sQuery(id+"F0.wireOp",EDGE,"E1");Q0=makeQuery(id+"F10.opBoolean","INTERSECT",EDGE,{"derivedFrom":[makeQuery(id+"F7.boolean.opBoolean","MERGE",FACE,{"derivedFrom":[makeQuery(id+"F1.opExtrude","SWEPT_FACE",FACE,{"disambiguationData":[OSD([subQ0])]}),makeQuery(id+"F7.opExtrude","SWEPT_FACE",FACE,{"disambiguationData":[OSD([subQ0])]})]}),makeQuery(id+"F9.opExtrude","SWEPT_FACE",FACE,{"disambiguationData":[OSD([sQuery(id+"F8.wireOp",EDGE,"E28.1")])]})]});}
            var Q1;
            {var subQ0=sQuery(id+"F0.wireOp",EDGE,"E1");Q1=makeQuery(id+"F10.opBoolean","INTERSECT",EDGE,{"derivedFrom":[makeQuery(id+"F7.boolean.opBoolean","MERGE",FACE,{"derivedFrom":[makeQuery(id+"F1.opExtrude","SWEPT_FACE",FACE,{"disambiguationData":[OSD([subQ0])]}),makeQuery(id+"F7.opExtrude","SWEPT_FACE",FACE,{"disambiguationData":[OSD([subQ0])]})]}),makeQuery(id+"F9.opExtrude","SWEPT_FACE",FACE,{"disambiguationData":[OSD([sQuery(id+"F8.wireOp",EDGE,"E26")])]})]});}
            var Q2;
            {var subQ0=sQuery(id+"F0.wireOp",EDGE,"E0");Q2=makeQuery(id+"F10.opBoolean","INTERSECT",EDGE,{"derivedFrom":[makeQuery(id+"F7.boolean.opBoolean","MERGE",FACE,{"derivedFrom":[makeQuery(id+"F1.opExtrude","SWEPT_FACE",FACE,{"disambiguationData":[OSD([subQ0])]}),makeQuery(id+"F7.opExtrude","SWEPT_FACE",FACE,{"disambiguationData":[OSD([subQ0])]})]}),makeQuery(id+"F9.opExtrude","SWEPT_FACE",FACE,{"disambiguationData":[OSD([sQuery(id+"F8.wireOp",EDGE,"E28.1")])]})]});}
            var Q3;
            {var subQ0=sQuery(id+"F0.wireOp",EDGE,"E0");Q3=makeQuery(id+"F10.opBoolean","INTERSECT",EDGE,{"derivedFrom":[makeQuery(id+"F7.boolean.opBoolean","MERGE",FACE,{"derivedFrom":[makeQuery(id+"F1.opExtrude","SWEPT_FACE",FACE,{"disambiguationData":[OSD([subQ0])]}),makeQuery(id+"F7.opExtrude","SWEPT_FACE",FACE,{"disambiguationData":[OSD([subQ0])]})]}),makeQuery(id+"F9.opExtrude","SWEPT_FACE",FACE,{"disambiguationData":[OSD([sQuery(id+"F8.wireOp",EDGE,"E26")])]})]});}
            var Q4;
            {var subQ0=sQuery(id+"F0.wireOp",EDGE,"E0");Q4=makeQuery(id+"F10.opBoolean","INTERSECT",EDGE,{"derivedFrom":[makeQuery(id+"F7.boolean.opBoolean","MERGE",FACE,{"derivedFrom":[makeQuery(id+"F1.opExtrude","SWEPT_FACE",FACE,{"disambiguationData":[OSD([subQ0])]}),makeQuery(id+"F7.opExtrude","SWEPT_FACE",FACE,{"disambiguationData":[OSD([subQ0])]})]}),makeQuery(id+"F9.opExtrude","SWEPT_FACE",FACE,{"disambiguationData":[OSD([sQuery(id+"F8.wireOp",EDGE,"E28.2")])]})]});}
            var Q5;
            {var subQ0=sQuery(id+"F0.wireOp",EDGE,"E0");Q5=makeQuery(id+"F10.opBoolean","INTERSECT",EDGE,{"derivedFrom":[makeQuery(id+"F7.boolean.opBoolean","MERGE",FACE,{"derivedFrom":[makeQuery(id+"F1.opExtrude","SWEPT_FACE",FACE,{"disambiguationData":[OSD([subQ0])]}),makeQuery(id+"F7.opExtrude","SWEPT_FACE",FACE,{"disambiguationData":[OSD([subQ0])]})]}),makeQuery(id+"F9.opExtrude","SWEPT_FACE",FACE,{"disambiguationData":[OSD([sQuery(id+"F8.wireOp",EDGE,"E25")])]})]});}
            var Q6;
            {var subQ0=sQuery(id+"F0.wireOp",EDGE,"E0");Q6=makeQuery(id+"F10.opBoolean","INTERSECT",EDGE,{"derivedFrom":[makeQuery(id+"F7.boolean.opBoolean","MERGE",FACE,{"derivedFrom":[makeQuery(id+"F1.opExtrude","SWEPT_FACE",FACE,{"disambiguationData":[OSD([subQ0])]}),makeQuery(id+"F7.opExtrude","SWEPT_FACE",FACE,{"disambiguationData":[OSD([subQ0])]})]}),makeQuery(id+"F9.opExtrude","SWEPT_FACE",FACE,{"disambiguationData":[OSD([sQuery(id+"F8.wireOp",EDGE,"E28.3")])]})]});}
            var Q7;
            {var subQ0=sQuery(id+"F0.wireOp",EDGE,"E0");Q7=makeQuery(id+"F10.opBoolean","INTERSECT",EDGE,{"derivedFrom":[makeQuery(id+"F7.boolean.opBoolean","MERGE",FACE,{"derivedFrom":[makeQuery(id+"F1.opExtrude","SWEPT_FACE",FACE,{"disambiguationData":[OSD([subQ0])]}),makeQuery(id+"F7.opExtrude","SWEPT_FACE",FACE,{"disambiguationData":[OSD([subQ0])]})]}),makeQuery(id+"F9.opExtrude","SWEPT_FACE",FACE,{"disambiguationData":[OSD([sQuery(id+"F8.wireOp",EDGE,"E24")])]})]});}
            var Q8;
            {var subQ0=sQuery(id+"F0.wireOp",EDGE,"E8");var subQ1=sQuery(id+"F0.wireOp",EDGE,"E0");Q8=makeQuery(id+"F14.opChamfer","BLEND_EDGE",EDGE,{"blendedFrom":[makeQuery(id+"F7.boolean.opBoolean","MERGE",EDGE,{"derivedFrom":[makeQuery(id+"F1.opExtrude","SWEPT_EDGE",EDGE,{"disambiguationData":[OSD([subQ1,subQ0])]}),makeQuery(id+"F7.opExtrude","SWEPT_EDGE",EDGE,{"disambiguationData":[OSD([subQ1,subQ0])]})]}),makeQuery(id+"F9.opExtrude","SWEPT_FACE",FACE,{"disambiguationData":[OSD([sQuery(id+"F8.wireOp",EDGE,"E24")])]})],"blendedInto":[makeQuery(id+"F9.opExtrude","SWEPT_FACE",FACE,{"disambiguationData":[OSD([sQuery(id+"F8.wireOp",EDGE,"E24")])]})]});}
            var Q9;
            {var subQ0=sQuery(id+"F0.wireOp",EDGE,"E8");Q9=makeQuery(id+"F10.opBoolean","INTERSECT",EDGE,{"derivedFrom":[makeQuery(id+"F7.boolean.opBoolean","MERGE",FACE,{"derivedFrom":[makeQuery(id+"F1.opExtrude","SWEPT_FACE",FACE,{"disambiguationData":[OSD([subQ0])]}),makeQuery(id+"F7.opExtrude","SWEPT_FACE",FACE,{"disambiguationData":[OSD([subQ0])]})]}),makeQuery(id+"F9.opExtrude","SWEPT_FACE",FACE,{"disambiguationData":[OSD([sQuery(id+"F8.wireOp",EDGE,"E24")])]})]});}
            var Q10;
            {var subQ0=sQuery(id+"F0.wireOp",EDGE,"E8");var subQ1=sQuery(id+"F0.wireOp",EDGE,"E7");Q10=makeQuery(id+"F14.opChamfer","BLEND_EDGE",EDGE,{"blendedFrom":[makeQuery(id+"F7.boolean.opBoolean","MERGE",EDGE,{"derivedFrom":[makeQuery(id+"F1.opExtrude","SWEPT_EDGE",EDGE,{"disambiguationData":[OSD([subQ1,subQ0])]}),makeQuery(id+"F7.opExtrude","SWEPT_EDGE",EDGE,{"disambiguationData":[OSD([subQ1,subQ0])]})]}),makeQuery(id+"F9.opExtrude","SWEPT_FACE",FACE,{"disambiguationData":[OSD([sQuery(id+"F8.wireOp",EDGE,"E24")])]})],"blendedInto":[makeQuery(id+"F9.opExtrude","SWEPT_FACE",FACE,{"disambiguationData":[OSD([sQuery(id+"F8.wireOp",EDGE,"E24")])]})]});}
            var Q11;
            {var subQ0=sQuery(id+"F0.wireOp",EDGE,"E7");Q11=makeQuery(id+"F10.opBoolean","INTERSECT",EDGE,{"derivedFrom":[makeQuery(id+"F7.boolean.opBoolean","MERGE",FACE,{"derivedFrom":[makeQuery(id+"F1.opExtrude","SWEPT_FACE",FACE,{"disambiguationData":[OSD([subQ0])]}),makeQuery(id+"F7.opExtrude","SWEPT_FACE",FACE,{"disambiguationData":[OSD([subQ0])]})]}),makeQuery(id+"F9.opExtrude","SWEPT_FACE",FACE,{"disambiguationData":[OSD([sQuery(id+"F8.wireOp",EDGE,"E28.3")])]})]});}
            var Q12;
            {var subQ0=sQuery(id+"F0.wireOp",EDGE,"E7");Q12=makeQuery(id+"F10.opBoolean","INTERSECT",EDGE,{"derivedFrom":[makeQuery(id+"F7.boolean.opBoolean","MERGE",FACE,{"derivedFrom":[makeQuery(id+"F1.opExtrude","SWEPT_FACE",FACE,{"disambiguationData":[OSD([subQ0])]}),makeQuery(id+"F7.opExtrude","SWEPT_FACE",FACE,{"disambiguationData":[OSD([subQ0])]})]}),makeQuery(id+"F9.opExtrude","SWEPT_FACE",FACE,{"disambiguationData":[OSD([sQuery(id+"F8.wireOp",EDGE,"E24")])]})]});}
            var Q13;
            {var subQ0=sQuery(id+"F0.wireOp",EDGE,"E7");Q13=makeQuery(id+"F10.opBoolean","INTERSECT",EDGE,{"derivedFrom":[makeQuery(id+"F7.boolean.opBoolean","MERGE",FACE,{"derivedFrom":[makeQuery(id+"F1.opExtrude","SWEPT_FACE",FACE,{"disambiguationData":[OSD([subQ0])]}),makeQuery(id+"F7.opExtrude","SWEPT_FACE",FACE,{"disambiguationData":[OSD([subQ0])]})]}),makeQuery(id+"F9.opExtrude","SWEPT_FACE",FACE,{"disambiguationData":[OSD([sQuery(id+"F8.wireOp",EDGE,"E28.2")])]})]});}
            var Q14;
            {var subQ0=sQuery(id+"F0.wireOp",EDGE,"E7");Q14=makeQuery(id+"F10.opBoolean","INTERSECT",EDGE,{"derivedFrom":[makeQuery(id+"F7.boolean.opBoolean","MERGE",FACE,{"derivedFrom":[makeQuery(id+"F1.opExtrude","SWEPT_FACE",FACE,{"disambiguationData":[OSD([subQ0])]}),makeQuery(id+"F7.opExtrude","SWEPT_FACE",FACE,{"disambiguationData":[OSD([subQ0])]})]}),makeQuery(id+"F9.opExtrude","SWEPT_FACE",FACE,{"disambiguationData":[OSD([sQuery(id+"F8.wireOp",EDGE,"E25")])]})]});}
            var Q15;
            {var subQ0=sQuery(id+"F0.wireOp",EDGE,"E7");Q15=makeQuery(id+"F10.opBoolean","INTERSECT",EDGE,{"derivedFrom":[makeQuery(id+"F7.boolean.opBoolean","MERGE",FACE,{"derivedFrom":[makeQuery(id+"F1.opExtrude","SWEPT_FACE",FACE,{"disambiguationData":[OSD([subQ0])]}),makeQuery(id+"F7.opExtrude","SWEPT_FACE",FACE,{"disambiguationData":[OSD([subQ0])]})]}),makeQuery(id+"F9.opExtrude","SWEPT_FACE",FACE,{"disambiguationData":[OSD([sQuery(id+"F8.wireOp",EDGE,"E28.1")])]})]});}
            var Q16;
            {var subQ0=sQuery(id+"F0.wireOp",EDGE,"E7");Q16=makeQuery(id+"F10.opBoolean","INTERSECT",EDGE,{"derivedFrom":[makeQuery(id+"F7.boolean.opBoolean","MERGE",FACE,{"derivedFrom":[makeQuery(id+"F1.opExtrude","SWEPT_FACE",FACE,{"disambiguationData":[OSD([subQ0])]}),makeQuery(id+"F7.opExtrude","SWEPT_FACE",FACE,{"disambiguationData":[OSD([subQ0])]})]}),makeQuery(id+"F9.opExtrude","SWEPT_FACE",FACE,{"disambiguationData":[OSD([sQuery(id+"F8.wireOp",EDGE,"E26")])]})]});}
            var Q17;
            {var subQ0=sQuery(id+"F0.wireOp",EDGE,"E7");Q17=makeQuery(id+"F10.opBoolean","INTERSECT",EDGE,{"derivedFrom":[makeQuery(id+"F7.boolean.opBoolean","MERGE",FACE,{"derivedFrom":[makeQuery(id+"F1.opExtrude","SWEPT_FACE",FACE,{"disambiguationData":[OSD([subQ0])]}),makeQuery(id+"F7.opExtrude","SWEPT_FACE",FACE,{"disambiguationData":[OSD([subQ0])]})]}),makeQuery(id+"F9.opExtrude","SWEPT_FACE",FACE,{"disambiguationData":[OSD([sQuery(id+"F8.wireOp",EDGE,"E28.0")])]})]});}
            var Q18;
            {var subQ0=sQuery(id+"F0.wireOp",EDGE,"E7");Q18=makeQuery(id+"F10.opBoolean","INTERSECT",EDGE,{"derivedFrom":[makeQuery(id+"F7.boolean.opBoolean","MERGE",FACE,{"derivedFrom":[makeQuery(id+"F1.opExtrude","SWEPT_FACE",FACE,{"disambiguationData":[OSD([subQ0])]}),makeQuery(id+"F7.opExtrude","SWEPT_FACE",FACE,{"disambiguationData":[OSD([subQ0])]})]}),makeQuery(id+"F9.opExtrude","SWEPT_FACE",FACE,{"disambiguationData":[OSD([sQuery(id+"F8.wireOp",EDGE,"E27")])]})]});}
            var Q19;
            {var subQ0=sQuery(id+"F0.wireOp",EDGE,"E6");Q19=makeQuery(id+"F10.opBoolean","INTERSECT",EDGE,{"derivedFrom":[makeQuery(id+"F7.boolean.opBoolean","MERGE",FACE,{"derivedFrom":[makeQuery(id+"F1.opExtrude","SWEPT_FACE",FACE,{"disambiguationData":[OSD([subQ0])]}),makeQuery(id+"F7.opExtrude","SWEPT_FACE",FACE,{"disambiguationData":[OSD([subQ0])]})]}),makeQuery(id+"F9.opExtrude","SWEPT_FACE",FACE,{"disambiguationData":[OSD([sQuery(id+"F8.wireOp",EDGE,"E27")])]})]});}
            var Q20;
            {var subQ0=sQuery(id+"F0.wireOp",EDGE,"E5");Q20=makeQuery(id+"F10.opBoolean","INTERSECT",EDGE,{"derivedFrom":[makeQuery(id+"F7.boolean.opBoolean","MERGE",FACE,{"derivedFrom":[makeQuery(id+"F1.opExtrude","SWEPT_FACE",FACE,{"disambiguationData":[OSD([subQ0])]}),makeQuery(id+"F7.opExtrude","SWEPT_FACE",FACE,{"disambiguationData":[OSD([subQ0])]})]}),makeQuery(id+"F9.opExtrude","SWEPT_FACE",FACE,{"disambiguationData":[OSD([sQuery(id+"F8.wireOp",EDGE,"E27")])]})]});}
            var Q21;
            {var subQ0=sQuery(id+"F0.wireOp",EDGE,"E4");Q21=makeQuery(id+"F10.opBoolean","INTERSECT",EDGE,{"derivedFrom":[makeQuery(id+"F7.boolean.opBoolean","MERGE",FACE,{"derivedFrom":[makeQuery(id+"F1.opExtrude","SWEPT_FACE",FACE,{"disambiguationData":[OSD([subQ0])]}),makeQuery(id+"F7.opExtrude","SWEPT_FACE",FACE,{"disambiguationData":[OSD([subQ0])]})]}),makeQuery(id+"F9.opExtrude","SWEPT_FACE",FACE,{"disambiguationData":[OSD([sQuery(id+"F8.wireOp",EDGE,"E27")])]})]});}
            var Q22;
            {var subQ0=sQuery(id+"F0.wireOp",EDGE,"E3");Q22=makeQuery(id+"F10.opBoolean","INTERSECT",EDGE,{"derivedFrom":[makeQuery(id+"F7.boolean.opBoolean","MERGE",FACE,{"derivedFrom":[makeQuery(id+"F1.opExtrude","SWEPT_FACE",FACE,{"disambiguationData":[OSD([subQ0])]}),makeQuery(id+"F7.opExtrude","SWEPT_FACE",FACE,{"disambiguationData":[OSD([subQ0])]})]}),makeQuery(id+"F9.opExtrude","SWEPT_FACE",FACE,{"disambiguationData":[OSD([sQuery(id+"F8.wireOp",EDGE,"E27")])]})]});}
            var Q23;
            {var subQ0=sQuery(id+"F0.wireOp",EDGE,"E2");Q23=makeQuery(id+"F10.opBoolean","INTERSECT",EDGE,{"derivedFrom":[makeQuery(id+"F7.boolean.opBoolean","MERGE",FACE,{"derivedFrom":[makeQuery(id+"F1.opExtrude","SWEPT_FACE",FACE,{"disambiguationData":[OSD([subQ0])]}),makeQuery(id+"F7.opExtrude","SWEPT_FACE",FACE,{"disambiguationData":[OSD([subQ0])]})]}),makeQuery(id+"F9.opExtrude","SWEPT_FACE",FACE,{"disambiguationData":[OSD([sQuery(id+"F8.wireOp",EDGE,"E27")])]})]});}
            var Q24;
            {var subQ0=sQuery(id+"F0.wireOp",EDGE,"E1");Q24=makeQuery(id+"F10.opBoolean","INTERSECT",EDGE,{"derivedFrom":[makeQuery(id+"F7.boolean.opBoolean","MERGE",FACE,{"derivedFrom":[makeQuery(id+"F1.opExtrude","SWEPT_FACE",FACE,{"disambiguationData":[OSD([subQ0])]}),makeQuery(id+"F7.opExtrude","SWEPT_FACE",FACE,{"disambiguationData":[OSD([subQ0])]})]}),makeQuery(id+"F9.opExtrude","SWEPT_FACE",FACE,{"disambiguationData":[OSD([sQuery(id+"F8.wireOp",EDGE,"E27")])]})]});}
            var Q25;
            {var subQ0=sQuery(id+"F0.wireOp",EDGE,"E1");Q25=makeQuery(id+"F10.opBoolean","INTERSECT",EDGE,{"derivedFrom":[makeQuery(id+"F7.boolean.opBoolean","MERGE",FACE,{"derivedFrom":[makeQuery(id+"F1.opExtrude","SWEPT_FACE",FACE,{"disambiguationData":[OSD([subQ0])]}),makeQuery(id+"F7.opExtrude","SWEPT_FACE",FACE,{"disambiguationData":[OSD([subQ0])]})]}),makeQuery(id+"F9.opExtrude","SWEPT_FACE",FACE,{"disambiguationData":[OSD([sQuery(id+"F8.wireOp",EDGE,"E28.0")])]})]});}
            var Q26;
            {var subQ0=sQuery(id+"F0.wireOp",EDGE,"E2");Q26=makeQuery(id+"F10.opBoolean","INTERSECT",EDGE,{"derivedFrom":[makeQuery(id+"F7.boolean.opBoolean","MERGE",FACE,{"derivedFrom":[makeQuery(id+"F1.opExtrude","SWEPT_FACE",FACE,{"disambiguationData":[OSD([subQ0])]}),makeQuery(id+"F7.opExtrude","SWEPT_FACE",FACE,{"disambiguationData":[OSD([subQ0])]})]}),makeQuery(id+"F9.opExtrude","SWEPT_FACE",FACE,{"disambiguationData":[OSD([sQuery(id+"F8.wireOp",EDGE,"E28.0")])]})]});}
            var Q27;
            {var subQ0=sQuery(id+"F0.wireOp",EDGE,"E3");Q27=makeQuery(id+"F10.opBoolean","INTERSECT",EDGE,{"derivedFrom":[makeQuery(id+"F7.boolean.opBoolean","MERGE",FACE,{"derivedFrom":[makeQuery(id+"F1.opExtrude","SWEPT_FACE",FACE,{"disambiguationData":[OSD([subQ0])]}),makeQuery(id+"F7.opExtrude","SWEPT_FACE",FACE,{"disambiguationData":[OSD([subQ0])]})]}),makeQuery(id+"F9.opExtrude","SWEPT_FACE",FACE,{"disambiguationData":[OSD([sQuery(id+"F8.wireOp",EDGE,"E28.0")])]})]});}
            chamfer(context, id + "F20", {"entities" : qUnion([Q0, Q1, Q2, Q3, Q4, Q5, Q6, Q7, Q8, Q9, Q10, Q11, Q12, Q13, Q14, Q15, Q16, Q17, Q18, Q19, Q20, Q21, Q22, Q23, Q24, Q25, Q26, Q27]), "width" : 0.2 * mm, "tangentPropagation" : true});
        }
        {
            var Q0;
            {var subQ0=sQuery(id+"F2.wireOp",EDGE,"E12.right");var subQ1=sQuery(id+"F2.wireOp",EDGE,"E12.bottom");Q0=makeQuery(id+"F7.boolean.opBoolean","MERGE",EDGE,{"derivedFrom":[makeQuery(id+"F6.opBoolean","COPY",EDGE,{"derivedFrom":makeQuery(id+"F4.opExtrude","SWEPT_EDGE",EDGE,{"disambiguationData":[OSD([subQ1,subQ0])]})}),makeQuery(id+"F7.opExtrude","SWEPT_EDGE",EDGE,{"disambiguationData":[OSD([sQuery(id+"F0.wireOp",EDGE,"E0"),sQuery(id+"F0.wireOp",EDGE,"E1"),sQuery(id+"F0.wireOp",EDGE,"E2"),sQuery(id+"F0.wireOp",EDGE,"E3"),sQuery(id+"F0.wireOp",EDGE,"E4"),sQuery(id+"F0.wireOp",EDGE,"E5"),sQuery(id+"F0.wireOp",EDGE,"E6"),sQuery(id+"F0.wireOp",EDGE,"E7"),sQuery(id+"F0.wireOp",EDGE,"E8"),subQ1,subQ0])]})]});}
            var Q1;
            {var subQ0=sQuery(id+"F2.wireOp",EDGE,"E12.bottom");var subQ1=sQuery(id+"F2.wireOp",EDGE,"E9.5");Q1=makeQuery(id+"F7.boolean.opBoolean","MERGE",EDGE,{"derivedFrom":[makeQuery(id+"F6.opBoolean","COPY",EDGE,{"derivedFrom":makeQuery(id+"F4.opExtrude","SWEPT_EDGE",EDGE,{"disambiguationData":[OSD([subQ1,subQ0])]})}),makeQuery(id+"F7.opExtrude","SWEPT_EDGE",EDGE,{"disambiguationData":[OSD([sQuery(id+"F0.wireOp",EDGE,"E0"),sQuery(id+"F0.wireOp",EDGE,"E1"),sQuery(id+"F0.wireOp",EDGE,"E2"),sQuery(id+"F0.wireOp",EDGE,"E3"),sQuery(id+"F0.wireOp",EDGE,"E4"),sQuery(id+"F0.wireOp",EDGE,"E5"),sQuery(id+"F0.wireOp",EDGE,"E6"),sQuery(id+"F0.wireOp",EDGE,"E7"),sQuery(id+"F0.wireOp",EDGE,"E8"),subQ1,subQ0])]})]});}
            chamfer(context, id + "F21", {"entities" : qUnion([Q0, Q1]), "width" : 0.5 * mm, "tangentPropagation" : true});
        }
    });
